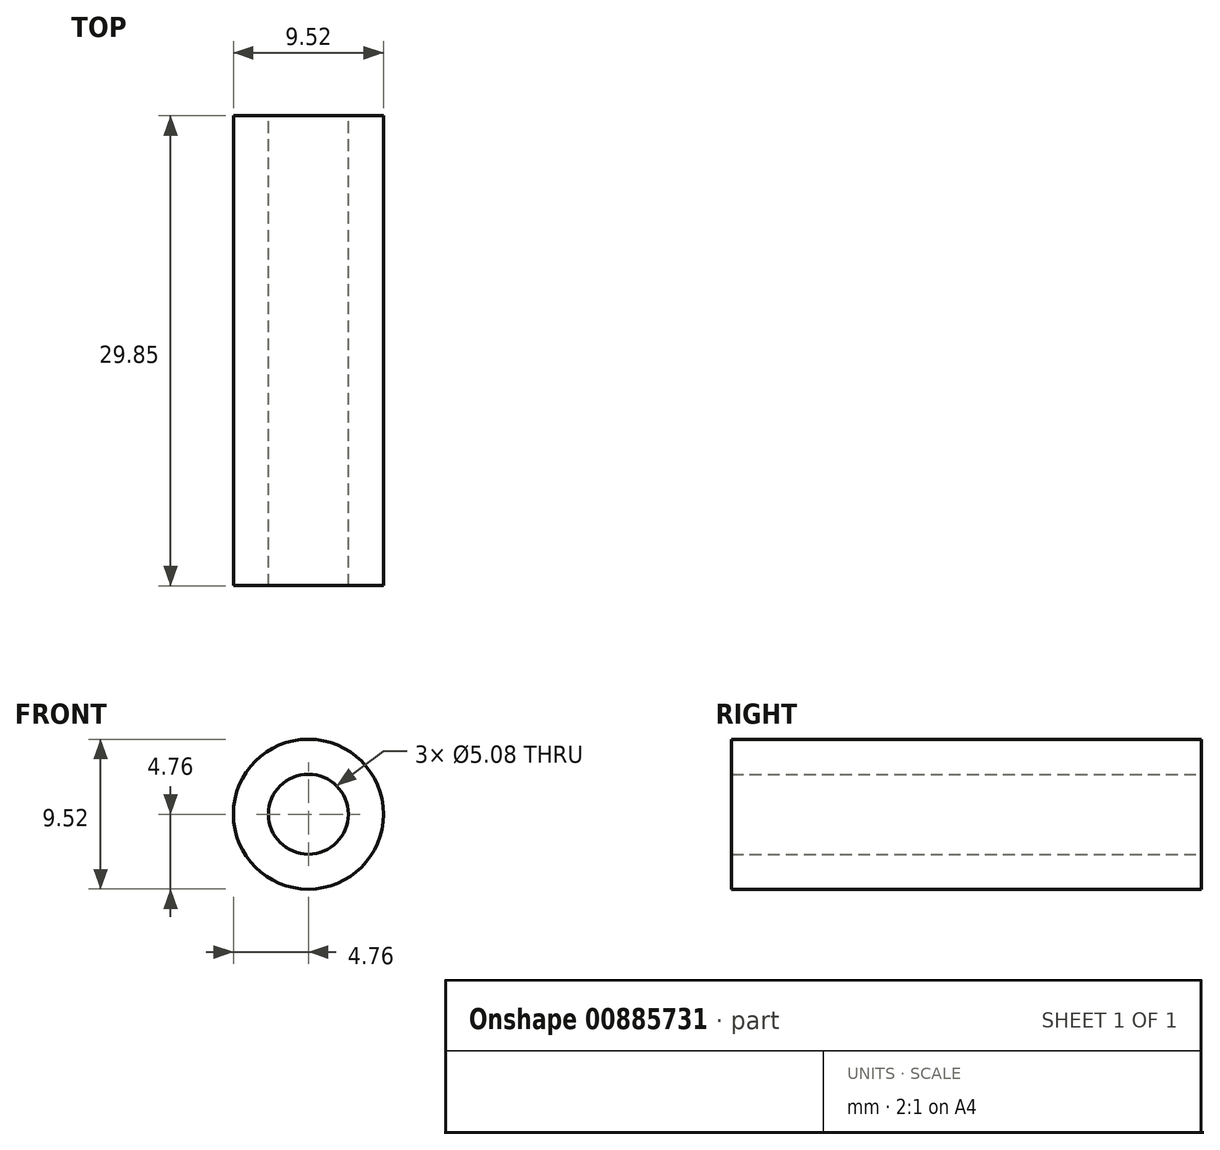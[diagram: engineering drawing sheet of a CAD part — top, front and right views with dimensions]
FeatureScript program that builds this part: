
annotation { "Feature Type Name" : "Feature", "Feature Type Description" : "" }
export const myFeature = defineFeature(function(context is Context, id is Id, definition is map)
    precondition{}
    {
        {
            var Q0;
            Q0=qCreatedBy(makeId("Front.planeOp"),FACE);
            var sketch = newSketch(context, id + "F0", { "sketchPlane" : qUnion([Q0])});
            skCircle(sketch, "E0", {"center": v(0, 0) * mm, "radius": 4.76 * mm});
            skCircle(sketch, "E1", {"center": v(0, 0) * mm, "radius": 2.54 * mm});
            skSolve(sketch);
        }
        {
            var Q0;
            Q0 = qSketchRegion(id + "F0", true);
            extrude(context, id + "F1", {"entities" : qUnion([Q0]), "depth" : 29.84 * mm, "offsetDistance" : 25.4 * mm});
        }
    });
